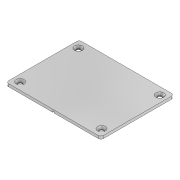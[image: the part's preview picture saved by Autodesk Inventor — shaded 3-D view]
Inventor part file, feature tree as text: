
AUTODESK INVENTOR PART (.ipt)
format: ipt  version: 2020 (Build 240168000, 168)  size: 131,584 bytes
history: native  units: mm
features: extrude x3, sketch x3, fillet x1, chamfer x1
ambient origin geometry x8: Origin, YZ Plane, XZ Plane, XY Plane, X Axis, Y Axis, Z Axis, Center Point
bodies: Solid1 (feature_tree)
feature tree (8):
  extrude  "Extrusion1"  Depth=54.0mm
  fillet  "Fillet1"  Radius=43.0mm
  extrude  "Extrusion2"  Depth=3.0mm
  extrude  "Extrusion3"  Depth=2.0mm
  chamfer  "Chamfer1"  Distance=3.0mm
  sketch  "Sketch1"  dims[d0=70.0mm d1=54.0mm d2=43.0mm]
  sketch  "Sketch2"  dims[d3=60.0mm d4=3.0mm]
  sketch  "Sketch3"  dims[d5=3.0mm d6=3.0mm d7=3.0mm d8=2.0mm d9=0.0mm d10=2.0mm d11=7.0mm d12=1.0mm d13=0.0mm d14=0.5mm d15=0.5mm d16=1.0mm d17=0.0mm d18=1.4mm d19=2.0mm d20=45.0deg]
